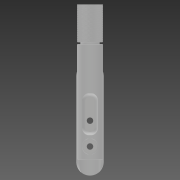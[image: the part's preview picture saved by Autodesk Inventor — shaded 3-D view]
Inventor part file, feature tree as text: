
AUTODESK INVENTOR PART (.ipt)
format: ipt  version: 2020 (Build 240168000, 168)  size: 19,207,680 bytes
history: native  units: in
note: dims shown in document units (in); Inventor stores cm internally (conversion verified against a paired STEP export)
features: other x23, extrude x12, fillet x5, projected_geometry x3, loft x2, pattern_circular x1, mirror x1, imported_body x1
ambient origin geometry x8: Origin, YZ Plane, XZ Plane, XY Plane, X Axis, Y Axis, Z Axis, Center Point
bodies: Solid1 (feature_tree), Solid2 (feature_tree), Solid3 (feature_tree), Solid6 (feature_tree), Solid4 (feature_tree), Solid5 (feature_tree)
feature tree (48):
  other  "strandberg-headless-tuner"
  other  "TunerTopView"
  other  "TunerFrontView"
  other  "TunerKnobPlane"
  other  "TunerKnobSep"
  other  "TunerEndPlane"
  other  "TunerEndProfile"
  loft  "TunerLoftFeature"
  loft  "TunerKnobLoftFeature"
  extrude  "TunerKnobSepFeature"  TaperAngle=0.0deg  [1 undecoded]
  fillet  "TunerFilletsFeature"  [1 undecoded]
  extrude  "TunerIndentFeature"  TaperAngle=0.0deg  [1 undecoded]
  fillet  "TunerIndentFillets1Feature"  Radius=0.03in
  fillet  "TunerIndentFillets2Feature"  Radius=0.01in
  other  "TunerIndentSubtractFeature"
  other  "TunderIndentProfile"
  extrude  "TunerHoleFeature"  Depth=0.05in
  extrude  "TunerHolesFeature"  Depth=0.05in
  other  "CountersinkPlane"
  extrude  "CountersinkFeature"  Depth=0.15in
  extrude  "BaseFeature"  Depth=0.25in TaperAngle=0.0deg
  extrude  "BaseExtendFeature"  Depth=0.12in
  extrude  "BaseFlareFeature"  Depth=0.1in
  fillet  "BaseFlareFilletsFeature"  Radius=1.8in
  extrude  "BaseHolesFeature"  Depth=0.4in
  other  "KnobSplitFeature"
  other  "KnurleCoilFeature"
  pattern_circular  "KnurleCoilRepeatFeature"  [2 undecoded]
  other  "KnobMidPlane"
  mirror  "KnurleMirrorFeature"
  extrude  "StringSaddleFeature"  Depth=0.2in TaperAngle=0.0deg
  extrude  "SaddleStringFeature"  [1 undecoded]
  fillet  "SaddleFilletFeature"  Radius=0.25in
  other  "CombineFeature"
  extrude  "MountHoleFeature"  Depth=1.0in TaperAngle=0.0deg
  other  "Edges1"
  other  "TunerIndent"
  projected_geometry  "Projected Loop1"
  other  "Countersink"
  imported_body  "Base"
  other  "BaseExtend"
  projected_geometry  "Projected Loop2"
  other  "BaseFlare"
  other  "BaseHoles"
  other  "KnurleCoil"
  projected_geometry  "Projected Loop3"
  other  "StringSaddle"
  other  "SaddleString"
note: 6 required parameter values undecoded (feature->parameter linkage not recoverable at this tier; creation-order binding heuristic only, values carry confidence <= 0.55)
